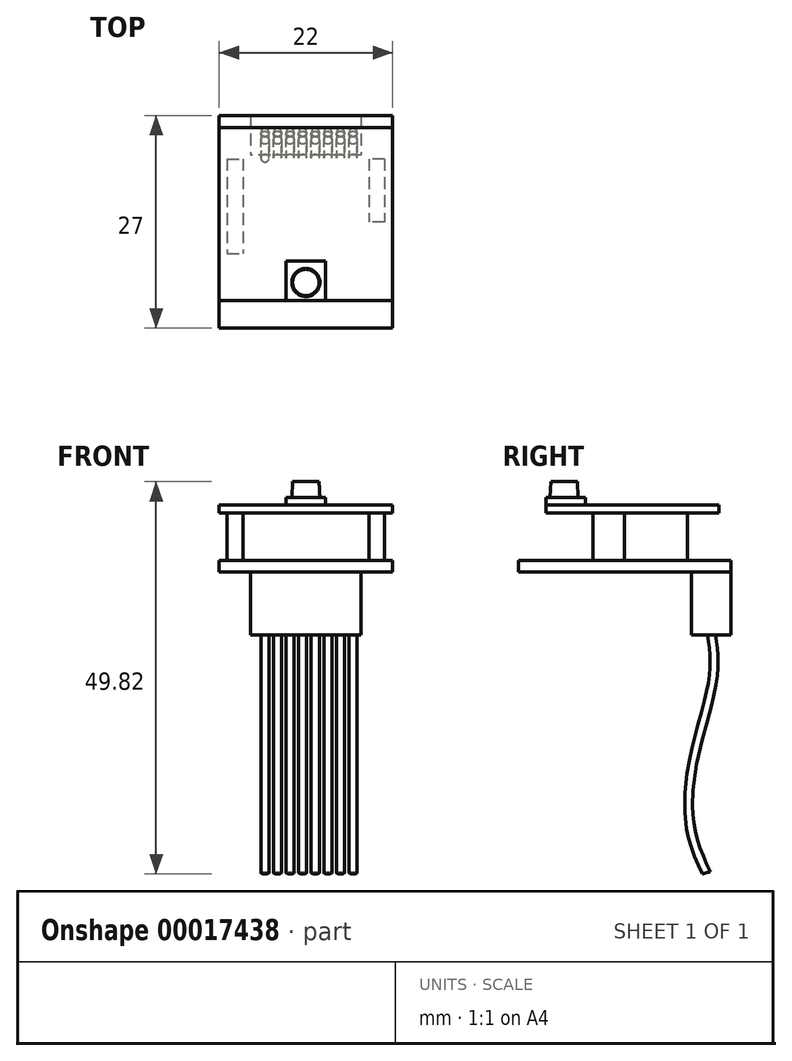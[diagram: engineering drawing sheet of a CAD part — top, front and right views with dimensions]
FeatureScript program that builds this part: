
annotation { "Feature Type Name" : "Feature", "Feature Type Description" : "" }
export const myFeature = defineFeature(function(context is Context, id is Id, definition is map)
    precondition{}
    {
        {
            var Q0;
            Q0=qCreatedBy(makeId("Top.planeOp"),FACE);
            var sketch = newSketch(context, id + "F0", { "sketchPlane" : qUnion([Q0])});
            skLineSegment(sketch, "E0.bottom", {"start": v(-11, 13.5) * mm, "end": v(11, 13.5) * mm});
            skLineSegment(sketch, "E0.top", {"start": v(-11, -13.5) * mm, "end": v(11, -13.5) * mm});
            skLineSegment(sketch, "E0.left", {"start": v(-11, 13.5) * mm, "end": v(-11, -13.5) * mm});
            skLineSegment(sketch, "E0.right", {"start": v(11, 13.5) * mm, "end": v(11, -13.5) * mm});
            skLineSegment(sketch, "E1", {"start": v(-11, 13.5) * mm, "end": v(11, -13.5) * mm, "construction": true});
            skSolve(sketch);
        }
        {
            var Q0;
            Q0=makeQuery(id+"F0.imprint","IMPRINT",FACE,{"disambiguationData":[TD([[makeQuery(id+"F0.imprint","IMPRINT",EDGE,{"derivedFrom":sQuery(id+"F0.wireOp",EDGE,"E0.bottom")}),-1.0]])]});
            extrude(context, id + "F1", {"entities" : qUnion([Q0]), "depth" : 1.5 * mm, "symmetric" : true});
        }
        {
            var Q0;
            Q0=makeQuery(id+"F1.opExtrude","CAP_FACE",FACE,{"disambiguationData":[OSD([sQuery(id+"F0.wireOp",EDGE,"E0.bottom"),sQuery(id+"F0.wireOp",EDGE,"E0.top"),sQuery(id+"F0.wireOp",EDGE,"E0.left"),sQuery(id+"F0.wireOp",EDGE,"E0.right")])],"isStart":true});
            var sketch = newSketch(context, id + "F2", { "sketchPlane" : qUnion([Q0])});
            skLineSegment(sketch, "E2.bottom", {"start": v(7, -13.5) * mm, "end": v(-7, -13.5) * mm});
            skLineSegment(sketch, "E2.top", {"start": v(7, -8.5) * mm, "end": v(-7, -8.5) * mm});
            skLineSegment(sketch, "E2.left", {"start": v(7, -13.5) * mm, "end": v(7, -8.5) * mm});
            skLineSegment(sketch, "E2.right", {"start": v(-7, -13.5) * mm, "end": v(-7, -8.5) * mm});
            skLineSegment(sketch, "E3", {"start": v(0, -8.5) * mm, "end": v(0, 0) * mm, "construction": true});
            skSolve(sketch);
        }
        {
            var Q0;
            Q0=makeQuery(id+"F2.imprint","IMPRINT",FACE,{"disambiguationData":[TD([[makeQuery(id+"F2.imprint","IMPRINT",EDGE,{"derivedFrom":sQuery(id+"F2.wireOp",EDGE,"E2.bottom")}),1.0]])]});
            extrude(context, id + "F3", {"entities" : qUnion([Q0]), "depth" : 8 * mm});
        }
        {
            var Q0;
            Q0=makeQuery(id+"F1.opExtrude","CAP_FACE",FACE,{"disambiguationData":[OSD([sQuery(id+"F0.wireOp",EDGE,"E0.bottom"),sQuery(id+"F0.wireOp",EDGE,"E0.top"),sQuery(id+"F0.wireOp",EDGE,"E0.left"),sQuery(id+"F0.wireOp",EDGE,"E0.right")])],"isStart":false});
            var sketch = newSketch(context, id + "F4", { "sketchPlane" : qUnion([Q0])});
            skLineSegment(sketch, "E4.bottom", {"start": v(-10, 8) * mm, "end": v(-8, 8) * mm});
            skLineSegment(sketch, "E4.top", {"start": v(-10, -4) * mm, "end": v(-8, -4) * mm});
            skLineSegment(sketch, "E4.left", {"start": v(-10, 8) * mm, "end": v(-10, -4) * mm});
            skLineSegment(sketch, "E4.right", {"start": v(-8, 8) * mm, "end": v(-8, -4) * mm});
            skLineSegment(sketch, "E5.bottom", {"start": v(10, 8) * mm, "end": v(8, 8) * mm});
            skLineSegment(sketch, "E5.top", {"start": v(10, 0) * mm, "end": v(8, 0) * mm});
            skLineSegment(sketch, "E5.left", {"start": v(10, 8) * mm, "end": v(10, 0) * mm});
            skLineSegment(sketch, "E5.right", {"start": v(8, 8) * mm, "end": v(8, 0) * mm});
            skSolve(sketch);
        }
        {
            var Q0;
            Q0=makeQuery(id+"F4.imprint","IMPRINT",FACE,{"disambiguationData":[TD([[makeQuery(id+"F4.imprint","IMPRINT",EDGE,{"derivedFrom":sQuery(id+"F4.wireOp",EDGE,"E4.bottom")}),-1.0]])]});
            var Q1;
            Q1=makeQuery(id+"F4.imprint","IMPRINT",FACE,{"disambiguationData":[TD([[makeQuery(id+"F4.imprint","IMPRINT",EDGE,{"derivedFrom":sQuery(id+"F4.wireOp",EDGE,"E5.bottom")}),1.0]])]});
            extrude(context, id + "F5", {"entities" : qUnion([Q0, Q1]), "depth" : 6 * mm});
        }
        {
            var Q0;
            Q0=makeQuery(id+"F5.opExtrude","CAP_FACE",FACE,{"disambiguationData":[OSD([sQuery(id+"F4.wireOp",EDGE,"E4.bottom"),sQuery(id+"F4.wireOp",EDGE,"E4.top"),sQuery(id+"F4.wireOp",EDGE,"E4.left"),sQuery(id+"F4.wireOp",EDGE,"E4.right")])],"isStart":false});
            var sketch = newSketch(context, id + "F6", { "sketchPlane" : qUnion([Q0])});
            skLineSegment(sketch, "E6.bottom", {"start": v(-11, 12) * mm, "end": v(11, 12) * mm});
            skLineSegment(sketch, "E6.top", {"start": v(-11, -10) * mm, "end": v(11, -10) * mm});
            skLineSegment(sketch, "E6.left", {"start": v(-11, 12) * mm, "end": v(-11, -10) * mm});
            skLineSegment(sketch, "E6.right", {"start": v(11, 12) * mm, "end": v(11, -10) * mm});
            skSolve(sketch);
        }
        {
            var Q0;
            Q0 = qSketchRegion(id + "F6", true);
            extrude(context, id + "F7", {"entities" : qUnion([Q0]), "depth" : 1 * mm});
        }
        {
            var Q0;
            Q0=makeQuery(id+"F7.opExtrude","CAP_FACE",FACE,{"disambiguationData":[OSD([sQuery(id+"F6.wireOp",EDGE,"E6.bottom"),sQuery(id+"F6.wireOp",EDGE,"E6.top"),sQuery(id+"F6.wireOp",EDGE,"E6.left"),sQuery(id+"F6.wireOp",EDGE,"E6.right")])],"isStart":false});
            var sketch = newSketch(context, id + "F8", { "sketchPlane" : qUnion([Q0])});
            skLineSegment(sketch, "E7.bottom", {"start": v(-2.5, -5) * mm, "end": v(2.5, -5) * mm});
            skLineSegment(sketch, "E7.top", {"start": v(-2.5, -10) * mm, "end": v(2.5, -10) * mm});
            skLineSegment(sketch, "E7.left", {"start": v(-2.5, -5) * mm, "end": v(-2.5, -10) * mm});
            skLineSegment(sketch, "E7.right", {"start": v(2.5, -5) * mm, "end": v(2.5, -10) * mm});
            skLineSegment(sketch, "E8", {"start": v(0, -5) * mm, "end": v(0, 0) * mm, "construction": true});
            skSolve(sketch);
        }
        {
            var Q0;
            Q0=makeQuery(id+"F8.imprint","IMPRINT",FACE,{"disambiguationData":[TD([[makeQuery(id+"F8.imprint","IMPRINT",EDGE,{"derivedFrom":sQuery(id+"F8.wireOp",EDGE,"E7.bottom")}),-1.0]])]});
            extrude(context, id + "F9", {"entities" : qUnion([Q0]), "depth" : 1 * mm});
        }
        {
            var Q0;
            Q0=makeQuery(id+"F9.opExtrude","CAP_FACE",FACE,{"disambiguationData":[OSD([sQuery(id+"F8.wireOp",EDGE,"E7.bottom"),sQuery(id+"F8.wireOp",EDGE,"E7.top"),sQuery(id+"F8.wireOp",EDGE,"E7.left"),sQuery(id+"F8.wireOp",EDGE,"E7.right")])],"isStart":false});
            var sketch = newSketch(context, id + "F10", { "sketchPlane" : qUnion([Q0])});
            skCircle(sketch, "E9", {"center": v(0, -7.7) * mm, "radius": 1.78 * mm});
            skSolve(sketch);
        }
        {
            var Q0;
            Q0=makeQuery(id+"F10.imprint","IMPRINT",FACE,{"disambiguationData":[TD([[makeQuery(id+"F10.imprint","IMPRINT",EDGE,{"derivedFrom":sQuery(id+"F10.wireOp",EDGE,"E9")}),1.0]])]});
            extrude(context, id + "F11", {"entities" : qUnion([Q0]), "operationType" : NewBodyOperationType.ADD, "depth" : 2 * mm, "hasDraft" : true, "draftAngle" : 3 * degree, "draftPullDirection" : true});
        }
        {
            var Q0;
            Q0=qCreatedBy(makeId("Right.planeOp"),FACE);
            var sketch = newSketch(context, id + "F12", { "sketchPlane" : qUnion([Q0])});
            skFitSpline(sketch, "E10", {"points": [v(11.23, -7.58) * mm, v(11.69, -13.78) * mm, v(9.39, -23.44) * mm, v(8.7, -32.86) * mm, v(10.77, -38.84) * mm], "startDerivative": vector(4.68, -26.53) * mm, "endDerivative": vector(11.54, -24.93) * mm});
            skSolve(sketch);
        }
        {
            var Q0;
            Q0=makeQuery(id+"F3.opExtrude","CAP_FACE",FACE,{"disambiguationData":[OSD([sQuery(id+"F2.wireOp",EDGE,"E2.bottom"),sQuery(id+"F2.wireOp",EDGE,"E2.top"),sQuery(id+"F2.wireOp",EDGE,"E2.left"),sQuery(id+"F2.wireOp",EDGE,"E2.right")])],"isStart":false});
            var sketch = newSketch(context, id + "F13", { "sketchPlane" : qUnion([Q0])});
            skCircle(sketch, "E11", {"center": v(6, -11.02) * mm, "radius": 0.51 * mm});
            skCircle(sketch, "E12.1.0.0", {"center": v(4.4, -11.02) * mm, "radius": 0.51 * mm});
            skCircle(sketch, "E12.2.0.0", {"center": v(2.8, -11.02) * mm, "radius": 0.51 * mm});
            skCircle(sketch, "E12.3.0.0", {"center": v(1.2, -11.02) * mm, "radius": 0.51 * mm});
            skCircle(sketch, "E12.4.0.0", {"center": v(-0.4, -11.02) * mm, "radius": 0.51 * mm});
            skCircle(sketch, "E12.5.0.0", {"center": v(-2, -11.02) * mm, "radius": 0.51 * mm});
            skCircle(sketch, "E12.6.0.0", {"center": v(-3.6, -11.02) * mm, "radius": 0.51 * mm});
            skCircle(sketch, "E12.7.0.0", {"center": v(-5.2, -11.02) * mm, "radius": 0.51 * mm});
            skLineSegment(sketch, "E12.direction1", {"start": v(6, -11.02) * mm, "end": v(4.4, -11.02) * mm, "construction": true});
            skSolve(sketch);
        }
        {
            var Q0;
            Q0 = qSketchRegion(id + "F13", true);
            var Q1;
            Q1=sQuery(id+"F12.wireOp",EDGE,"E10");
            sweep(context, id + "F14", {"operationType" : NewBodyOperationType.ADD, "profiles" : qUnion([Q0]), "path" : qUnion([Q1])});
        }
    });
